# Revit family: NAU_Naughtone_Stng_Lasso_3SeatStoolWIP4
name_source: partatom
category: Furniture
revit_build: Autodesk Revit 2016 (Build: 20150714_1515(x64)
units: mm (PartAtom-declared; Revit-internal decimal feet)

## family parameters
Always vertical = Yes
Cut with Voids When Loaded = No
OmniClass Number = 23.40.20.00
OmniClass Title = General Furniture and Specialties
Room Calculation Point = No
Shared = Yes
Work Plane-Based = No

## types (2) — shared parameters
Assembly Code = E2020200
AssetType = Movable
Category = Pr_40_50_12 : Chairs, seats and benches
DurationUnit = year
ExpectedLife = 7
FrameMaterial = NAU_Generic_Metal_Black
IfcExportAs = IfcFurnishingElementType
IfcExportType = CHAIR
Keynote = Pr_40_50_12
ManufacturerName = Naughtone
ManufacturerURL = www.naughtone.com
NBSDescription = Seating
NBSReference = 45-35-72/352
ProductInformation = www.naughtone.com/products/lasso
SustainabilityPerformance = FSC certifeied, SCS indoor advantage gold
URL = www.naughtone.com
Uniclass2015Code = Pr_40_50_12
Uniclass2015Title = Chairs, seats and benches
Uniclass2015Version = Products v1.14
Version = 1
WarrantyDurationLabor = 7
WarrantyDurationParts = 7
WarrantyDurationUnit = year

## per-type parameters (varying)
| type | BIMObjectName | Description | Finish | IsTable | Material | Model | ModelNumber | ModelReference | Name | NominalHeight | NominalLength | NominalWidth | Size |
| Lasso 3 Seat Stool LAS3S 1210 x 1210 x 500 mm | NAU_Naughtone_Seating_Lasso_3SeatStool | Lasso 3 seat stool - Lasso is a collaborative seating and table system that can be easily moved to create clusters around the three seat stool. | Fabric upholstery, white/black/RAL EPC steel ring | No | Fabric, plywood frame, foam, wooden table top | LAS3S | LAS3S | Lasso 3 seat stool - Lasso is a collaborative seating and table system that can be easily moved to create clusters around the three seat stool. | Seating_Lasso_3SeatStool_Naughtone | 500 mm  [stored 1.64042 ft] | 1210 mm  [stored 3.96982 ft] | 1210 mm  [stored 3.96982 ft] | 1210 x 1210 x 500 mm |
| Lasso 3 Seat Stool and Tables LAS3STAB 1425 x 1465 x 705 mm | NAU_Naughtone_Seating_Lasso_3SeatStoolandTables | Lasso 3 seat stool and tables - Lasso is a collaborative seating and table system that can be easily moved to create clusters around the three seat stool. | Fabric upholstery, wooden table top with oak/walnut veneer, white/black MFMDF top with reverse chamfer, white/black/RAL EPC steel ring | Yes | Fabric, plywood frame, foam, steel ring, wooden table top | LAS3STAB | LAS3STAB | Lasso 3 seat stool and tables - Lasso is a collaborative seating and table system that can be easily moved to create clusters around the three seat stool. | Seating_Lasso_3SeatStoolandTables_Naughtone | 705 mm  [stored 2.31299 ft] | 1425 mm  [stored 4.6752 ft] | 1465 mm  [stored 4.80643 ft] | 1425 x 1465 x 705 mm |

note: [stored X ft] marks values corroborated as IEEE doubles in the binary element streams (Revit-internal decimal feet)

## geometry (parser evidence)
native form markers: Sweep x2
no freeform markers — native parametric forms only
